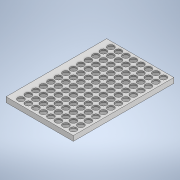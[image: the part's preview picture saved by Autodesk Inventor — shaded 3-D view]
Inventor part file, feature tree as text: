
AUTODESK INVENTOR PART (.ipt)
format: ipt  version: 2020 (Build 240168000, 168)  size: 280,064 bytes
history: native  units: in
note: dims shown in document units (in); Inventor stores cm internally (conversion verified against a paired STEP export)
features: sketch x2, extrude x1, hole x1, pattern_linear x1
ambient origin geometry x8: Origin, YZ Plane, XZ Plane, XY Plane, X Axis, Y Axis, Z Axis, Center Point
bodies: Solid1 (feature_tree)
feature tree (5):
  extrude  "Extrusion1"  Depth=5.0299in
  hole  "Hole1"  [1 undecoded]
  pattern_linear  "Rectangular Pattern1"  Spacing1=0.25in  [1 undecoded]
  sketch  "Sketch1"  dims[d0=3.3654in d1=5.0299in]
  sketch  "Sketch2"  dims[d3=45.0deg d4=0.375in d5=0.25in d6=0.0in d7=0.375in d8=135.0deg d9=0.375in d10=0.3125in d11=0.75in d12=0.332in d13=0.25in d14=0.5635in d15=0.0625in d16=0.8108in d17=3.1496in d19=0.375in d20=5.1181in d22=0.375in]
note: 2 required parameter values undecoded (feature->parameter linkage not recoverable at this tier; creation-order binding heuristic only, values carry confidence <= 0.55)
